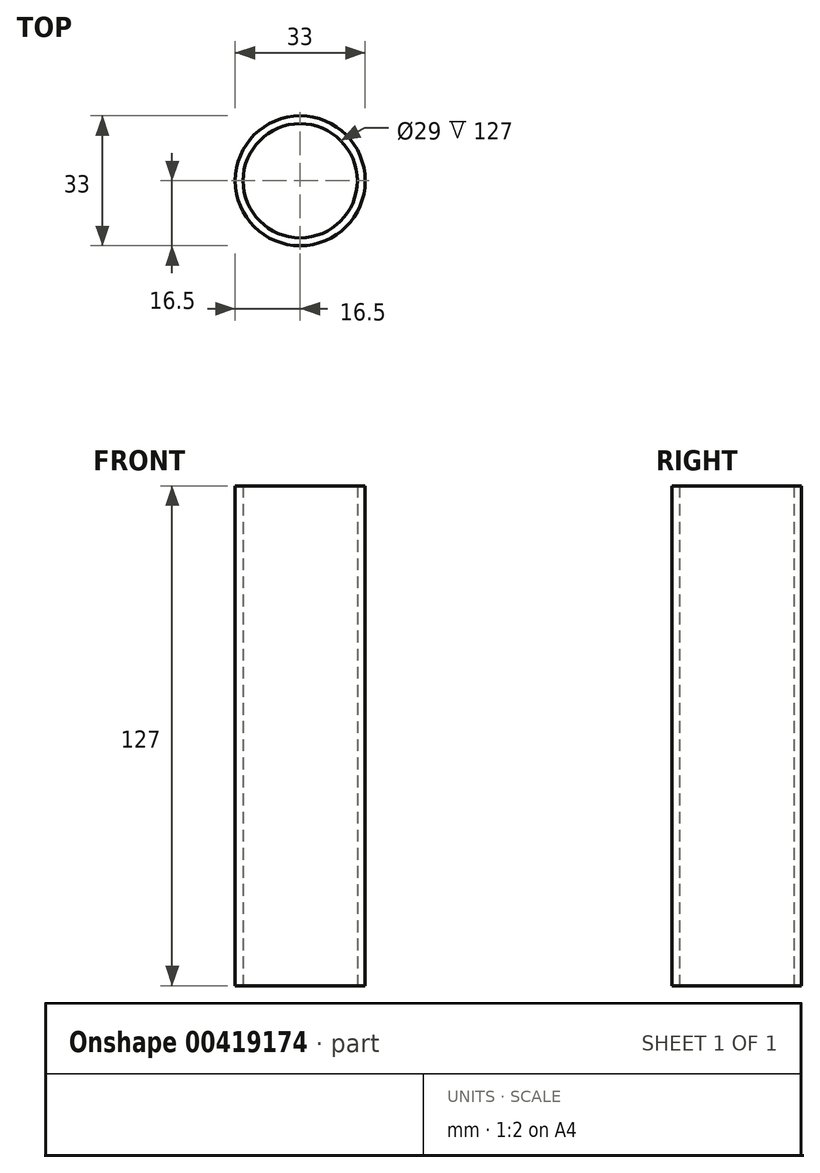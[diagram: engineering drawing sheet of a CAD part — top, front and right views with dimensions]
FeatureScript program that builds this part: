
annotation { "Feature Type Name" : "Feature", "Feature Type Description" : "" }
export const myFeature = defineFeature(function(context is Context, id is Id, definition is map)
    precondition{}
    {
        {
            var Q0;
            Q0=qCreatedBy(makeId("Top.planeOp"),FACE);
            var sketch = newSketch(context, id + "F0", { "sketchPlane" : qUnion([Q0])});
            skCircle(sketch, "E0", {"center": v(0, 0) * mm, "radius": 14.5 * mm});
            skCircle(sketch, "E1", {"center": v(0, 0) * mm, "radius": 16.5 * mm});
            skSolve(sketch);
        }
        {
            var Q0;
            Q0 = qSketchRegion(id + "F0", true);
            extrude(context, id + "F1", {"entities" : qUnion([Q0]), "depth" : 127 * mm});
        }
    });
